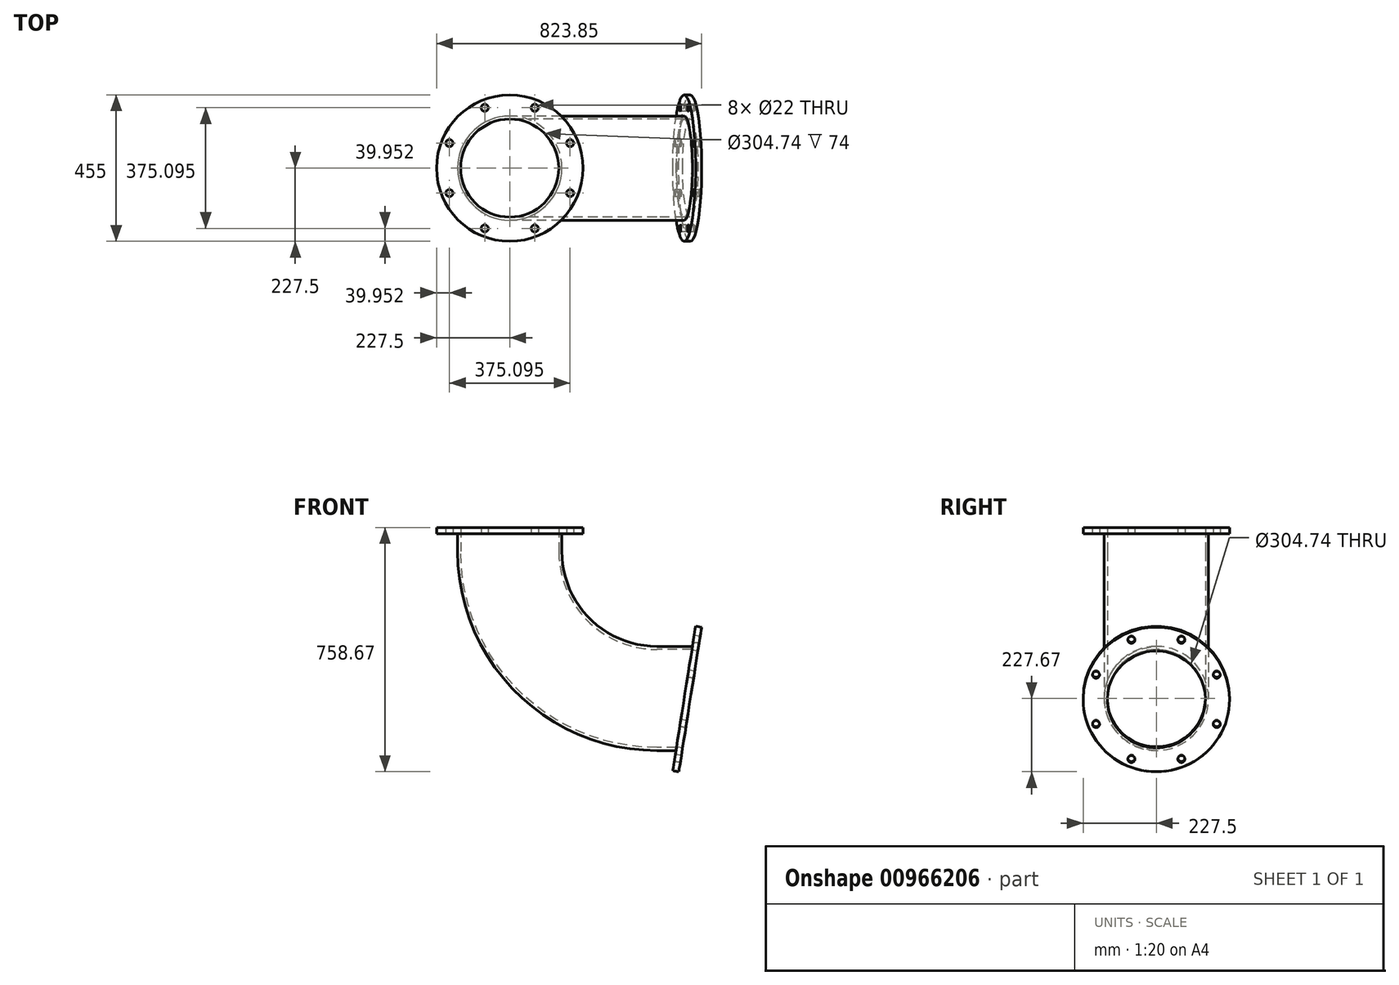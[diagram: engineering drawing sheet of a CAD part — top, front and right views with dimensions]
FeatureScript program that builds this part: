
annotation { "Feature Type Name" : "Feature", "Feature Type Description" : "" }
export const myFeature = defineFeature(function(context is Context, id is Id, definition is map)
    precondition{}
    {
        {
            var Q0;
            Q0=qCreatedBy(makeId("Top.planeOp"),FACE);
            var sketch = newSketch(context, id + "F0", { "sketchPlane" : qUnion([Q0])});
            skCircle(sketch, "E0", {"center": v(0, 0) * mm, "radius": 161.9 * mm});
            skCircle(sketch, "E1", {"center": v(0, 0) * mm, "radius": 152.37 * mm});
            skSolve(sketch);
        }
        {
            var Q0;
            Q0=qCreatedBy(makeId("Front.planeOp"),FACE);
            var sketch = newSketch(context, id + "F1", { "sketchPlane" : qUnion([Q0])});
            skLineSegment(sketch, "E2", {"start": v(0, 0) * mm, "end": v(457, 0) * mm, "construction": true});
            skArc(sketch, "E3", {"start": v(0, 0) * mm, "mid": v(133.85, -323.15) * mm, "end": v(457, -457) * mm});
            skSolve(sketch);
        }
        {
            var Q0;
            Q0 = qSketchRegion(id + "F0", true);
            var Q1;
            Q1 = qConstructionFilter(qBodyType(qCreatedBy(id + "F1" ,EDGE), BodyType.WIRE), ConstructionObject.NO);
            sweep(context, id + "F2", {"profiles" : qUnion([Q0]), "path" : qUnion([Q1])});
        }
        {
            var Q0;
            Q0=makeQuery(id+"F2.opSweep","CAP_FACE",FACE,{"disambiguationData":[OSD([sQuery(id+"F0.wireOp",EDGE,"E0"),sQuery(id+"F0.wireOp",EDGE,"E1"),sQuery(id+"F1.wireOp",VERTEX,"E3.end")])],"isStart":false});
            cPlane(context, id + "F3", {"entities" : qUnion([Q0]), "cplaneType" : CPlaneType.OFFSET, "offset" : 85 * mm, "width" : 150 * mm, "height" : 150 * mm});
        }
        {
            var Q0;
            Q0=qCreatedBy(id+"F3.planeOp",FACE);
            var sketch = newSketch(context, id + "F4", { "sketchPlane" : qUnion([Q0])});
            skLineSegment(sketch, "E4", {"start": v(0, -457) * mm, "end": v(314.46, -457) * mm, "construction": true});
            skSolve(sketch);
        }
        {
            var Q0;
            Q0=qCreatedBy(id+"F3.planeOp",FACE);
            var Q1;
            Q1=sQuery(id+"F4.wireOp",EDGE,"E4");
            cPlane(context, id + "F5", {"entities" : qUnion([Q0, Q1]), "cplaneType" : CPlaneType.LINE_ANGLE, "offset" : 25 * mm, "angle" : 9 * degree, "width" : 150 * mm, "height" : 150 * mm});
        }
        {
            var Q0;
            Q0=makeQuery(id+"F2.opSweep","CAP_FACE",FACE,{"disambiguationData":[OSD([sQuery(id+"F0.wireOp",EDGE,"E0"),sQuery(id+"F0.wireOp",EDGE,"E1"),sQuery(id+"F1.wireOp",VERTEX,"E3.end")])],"isStart":false});
            var sketch = newSketch(context, id + "F6", { "sketchPlane" : qUnion([Q0])});
            skCircle(sketch, "E5", {"center": v(0, -457) * mm, "radius": 161.9 * mm});
            skCircle(sketch, "E6", {"center": v(0, -457) * mm, "radius": 152.37 * mm});
            skSolve(sketch);
        }
        {
            var Q0;
            Q0 = qSketchRegion(id + "F6", true);
            var Q1;
            Q1=qCreatedBy(id+"F5.planeOp",FACE);
            extrude(context, id + "F7", {"entities" : qUnion([Q0]), "operationType" : NewBodyOperationType.ADD, "endBound" : BoundingType.UP_TO_SURFACE, "depth" : 25 * mm, "endBoundEntityFace" : qUnion([Q1]), "offsetDistance" : 25 * mm});
        }
        {
            var Q0;
            Q0=makeQuery(id+"F7.opExtrude","CAP_FACE",FACE,{"disambiguationData":[OSD([sQuery(id+"F6.wireOp",EDGE,"E5"),sQuery(id+"F6.wireOp",EDGE,"E6")])],"isStart":false});
            var sketch = newSketch(context, id + "F8", { "sketchPlane" : qUnion([Q0])});
            skCircle(sketch, "E7", {"center": v(0, -366.59) * mm, "radius": 152.37 * mm});
            skCircle(sketch, "E8", {"center": v(0, -366.59) * mm, "radius": 227.5 * mm});
            skCircle(sketch, "E9", {"center": v(0, -366.59) * mm, "radius": 203 * mm, "construction": true});
            skPoint(sketch, "E10.endSnap0", {"position": v(0, -202.67) * mm});
            skCircle(sketch, "E11", {"center": v(77.68, -179.04) * mm, "radius": 11 * mm});
            skCircle(sketch, "E12.1.0", {"center": v(-77.68, -179.04) * mm, "radius": 11 * mm});
            skCircle(sketch, "E12.2.0", {"center": v(-187.55, -288.9) * mm, "radius": 11 * mm});
            skCircle(sketch, "E12.3.0", {"center": v(-187.55, -444.27) * mm, "radius": 11 * mm});
            skCircle(sketch, "E12.4.0", {"center": v(-77.68, -554.13) * mm, "radius": 11 * mm});
            skCircle(sketch, "E12.5.0", {"center": v(77.68, -554.13) * mm, "radius": 11 * mm});
            skCircle(sketch, "E12.6.0", {"center": v(187.55, -444.27) * mm, "radius": 11 * mm});
            skCircle(sketch, "E12.7.0", {"center": v(187.55, -288.9) * mm, "radius": 11 * mm});
            skSolve(sketch);
        }
        {
            var Q0;
            Q0 = qSketchRegion(id + "F8", true);
            extrude(context, id + "F9", {"entities" : qUnion([Q0]), "operationType" : NewBodyOperationType.ADD, "depth" : 19 * mm, "offsetDistance" : 25 * mm});
        }
        {
            var Q0;
            Q0=makeQuery(id+"F2.opSweep","CAP_FACE",FACE,{"disambiguationData":[OSD([sQuery(id+"F0.wireOp",EDGE,"E0"),sQuery(id+"F0.wireOp",EDGE,"E1"),sQuery(id+"F1.wireOp",VERTEX,"E3.start")])],"isStart":true});
            var sketch = newSketch(context, id + "F10", { "sketchPlane" : qUnion([Q0])});
            skCircle(sketch, "E13", {"center": v(0, 0) * mm, "radius": 161.9 * mm});
            skCircle(sketch, "E14", {"center": v(0, 0) * mm, "radius": 152.37 * mm});
            skSolve(sketch);
        }
        {
            var Q0;
            Q0 = qSketchRegion(id + "F10", true);
            var Q1;
            Q1 = qConstructionFilter(qBodyType(qCreatedBy(id + "F10" ,EDGE), BodyType.WIRE), ConstructionObject.NO);
            extrude(context, id + "F11", {"entities" : qUnion([Q0]), "operationType" : NewBodyOperationType.ADD, "surfaceOperationType" : NewSurfaceOperationType.ADD, "surfaceEntities" : qUnion([Q1]), "depth" : 55 * mm, "offsetDistance" : 25 * mm});
        }
        {
            var Q0;
            Q0=makeQuery(id+"F11.opExtrude","CAP_FACE",FACE,{"disambiguationData":[OSD([sQuery(id+"F10.wireOp",EDGE,"E13"),sQuery(id+"F10.wireOp",EDGE,"E14")])],"isStart":false});
            var sketch = newSketch(context, id + "F12", { "sketchPlane" : qUnion([Q0])});
            skCircle(sketch, "E15", {"center": v(0, 0) * mm, "radius": 152.37 * mm});
            skCircle(sketch, "E16", {"center": v(0, 0) * mm, "radius": 227.5 * mm});
            skCircle(sketch, "E17", {"center": v(0, 0) * mm, "radius": 203 * mm, "construction": true});
            skPoint(sketch, "E18.endSnap0", {"position": v(-0.92, 174.12) * mm});
            skCircle(sketch, "E19", {"center": v(77.68, 187.55) * mm, "radius": 11 * mm});
            skCircle(sketch, "E20.1.0", {"center": v(-77.68, 187.55) * mm, "radius": 11 * mm});
            skCircle(sketch, "E20.2.0", {"center": v(-187.55, 77.68) * mm, "radius": 11 * mm});
            skCircle(sketch, "E20.3.0", {"center": v(-187.55, -77.68) * mm, "radius": 11 * mm});
            skCircle(sketch, "E20.4.0", {"center": v(-77.68, -187.55) * mm, "radius": 11 * mm});
            skCircle(sketch, "E20.5.0", {"center": v(77.68, -187.55) * mm, "radius": 11 * mm});
            skCircle(sketch, "E20.6.0", {"center": v(187.55, -77.68) * mm, "radius": 11 * mm});
            skCircle(sketch, "E20.7.0", {"center": v(187.55, 77.68) * mm, "radius": 11 * mm});
            skSolve(sketch);
        }
        {
            var Q0;
            Q0 = qSketchRegion(id + "F12", true);
            extrude(context, id + "F13", {"entities" : qUnion([Q0]), "operationType" : NewBodyOperationType.ADD, "depth" : 19 * mm, "offsetDistance" : 25 * mm});
        }
    });
